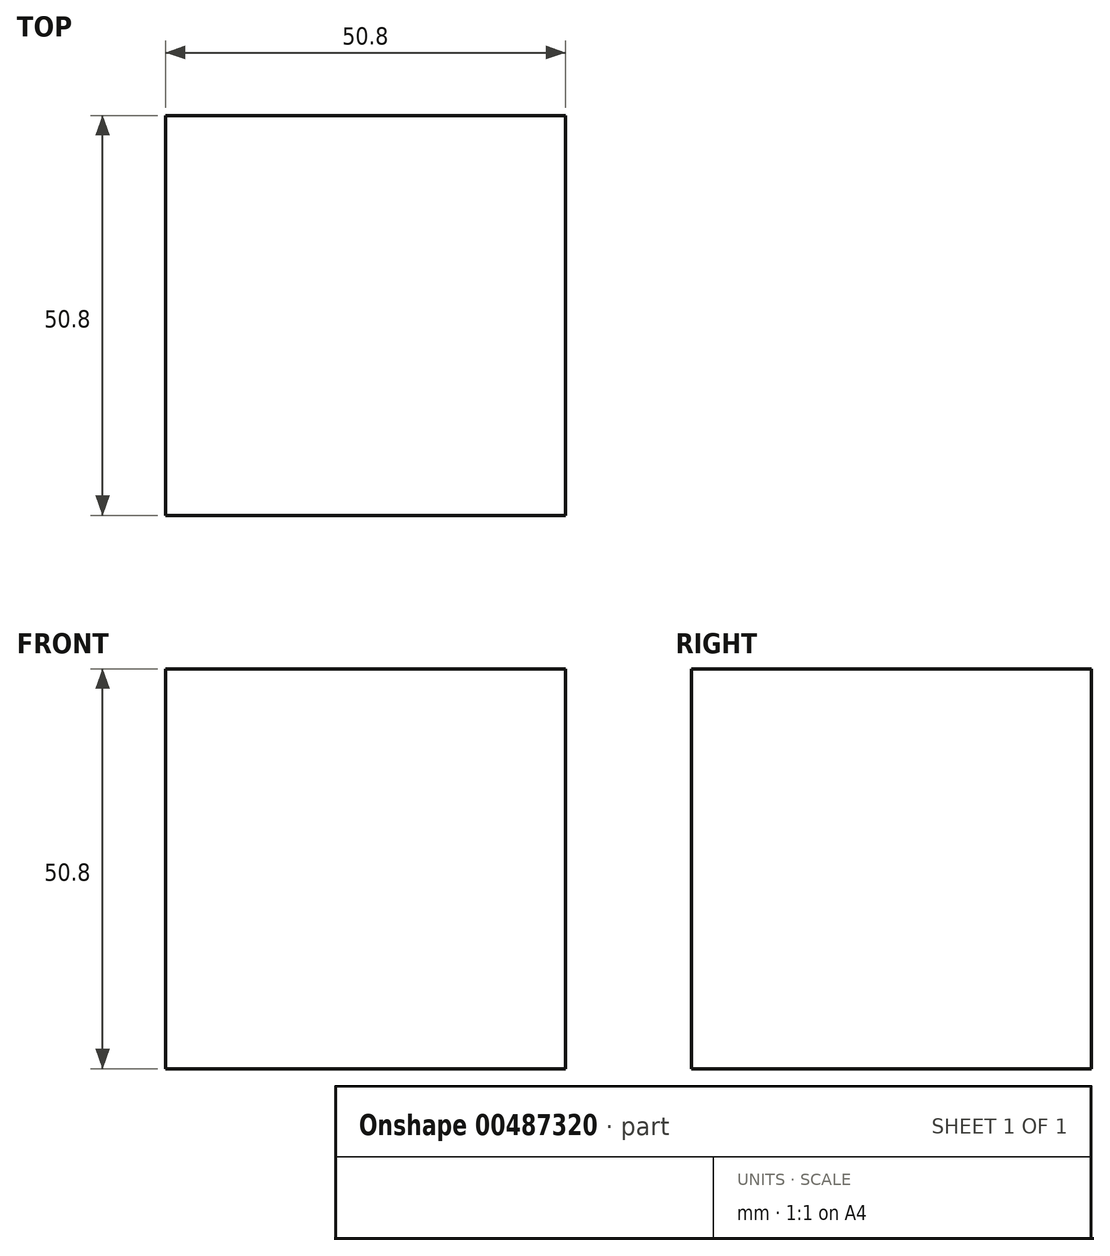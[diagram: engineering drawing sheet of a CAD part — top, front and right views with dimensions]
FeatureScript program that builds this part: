
annotation { "Feature Type Name" : "Feature", "Feature Type Description" : "" }
export const myFeature = defineFeature(function(context is Context, id is Id, definition is map)
    precondition{}
    {
        {
            var Q0;
            Q0=qCreatedBy(makeId("Front.planeOp"),FACE);
            var sketch = newSketch(context, id + "F0", { "sketchPlane" : qUnion([Q0])});
            skLineSegment(sketch, "E0.bottom", {"start": v(0, 0) * mm, "end": v(50.8, 0) * mm});
            skLineSegment(sketch, "E0.top", {"start": v(0, -50.8) * mm, "end": v(50.8, -50.8) * mm});
            skLineSegment(sketch, "E0.left", {"start": v(0, 0) * mm, "end": v(0, -50.8) * mm});
            skLineSegment(sketch, "E0.right", {"start": v(50.8, 0) * mm, "end": v(50.8, -50.8) * mm});
            skSolve(sketch);
        }
        {
            var Q0;
            Q0 = qSketchRegion(id + "F0", true);
            extrude(context, id + "F1", {"entities" : qUnion([Q0]), "depth" : 50.8 * mm});
        }
    });
